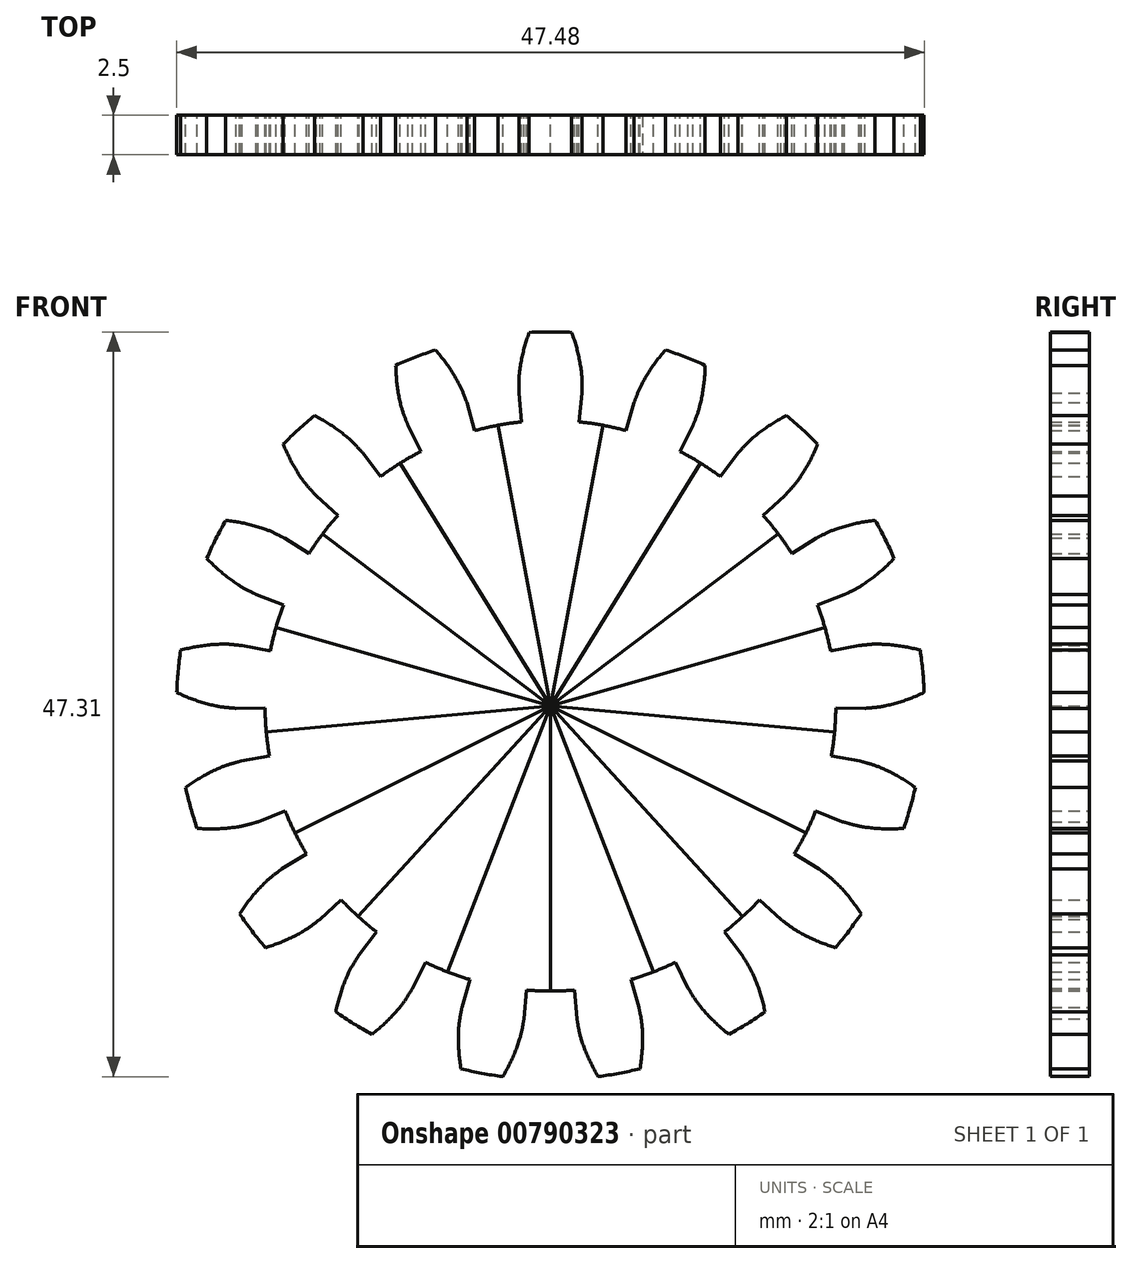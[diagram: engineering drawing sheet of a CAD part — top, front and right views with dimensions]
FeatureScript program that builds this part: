
annotation { "Feature Type Name" : "Feature", "Feature Type Description" : "" }
export const myFeature = defineFeature(function(context is Context, id is Id, definition is map)
    precondition{}
    {
        {
            var Q0;
            Q0=qCreatedBy(makeId("Front.planeOp"),FACE);
            var sketch = newSketch(context, id + "F0", { "sketchPlane" : qUnion([Q0])});
            skArc(sketch, "E0", {"start": v(1.97, 21.16) * mm, "mid": v(1.97, 21.16) * mm, "end": v(1.96, 21.16) * mm});
            skArc(sketch, "E1.0", {"start": v(1.35, 23.71) * mm, "mid": v(0, 23.75) * mm, "end": v(-1.35, 23.71) * mm});
            skArc(sketch, "E2.0", {"start": v(3.33, 17.82) * mm, "mid": v(2.58, 17.94) * mm, "end": v(1.83, 18.03) * mm});
            skPoint(sketch, "E3", {"position": v(-1.96, 21.16) * mm});
            skPoint(sketch, "E4", {"position": v(-2.01, 19.87) * mm});
            skFitSpline(sketch, "E5", {"points": [v(-2.01, 19.87) * mm, v(-2, 20.04) * mm, v(-2, 20.55) * mm, v(-1.94, 21.4) * mm, v(-1.71, 22.55) * mm, v(-1.35, 23.71) * mm], "startDerivative": vector(0.13, 1.6) * mm, "endDerivative": vector(1.85, 5.2) * mm});
            skLineSegment(sketch, "E6", {"start": v(-2.01, 19.87) * mm, "end": v(-1.83, 18.03) * mm});
            skLineSegment(sketch, "E7", {"start": v(-1.83, 18.03) * mm, "end": v(-3.33, 17.82) * mm});
            skFitSpline(sketch, "E8.MirrorCS", {"points": [v(2.01, 19.87) * mm, v(2, 20.04) * mm, v(2, 20.55) * mm, v(1.94, 21.4) * mm, v(1.71, 22.55) * mm, v(1.35, 23.71) * mm], "startDerivative": vector(-0.13, 1.6) * mm, "endDerivative": vector(-1.85, 5.2) * mm});
            skLineSegment(sketch, "E9.MirrorCS", {"start": v(1.83, 18.03) * mm, "end": v(3.33, 17.82) * mm});
            skLineSegment(sketch, "E10.MirrorCS", {"start": v(2.01, 19.87) * mm, "end": v(1.83, 18.03) * mm});
            skPoint(sketch, "E11.MirrorP", {"position": v(1.96, 21.16) * mm});
            skLineSegment(sketch, "E12", {"start": v(0, 0) * mm, "end": v(-3.33, 17.82) * mm});
            skLineSegment(sketch, "E13", {"start": v(0, 0) * mm, "end": v(3.33, 17.82) * mm});
            skArc(sketch, "E14.trimOffspring", {"start": v(-1.83, 18.03) * mm, "mid": v(-2.58, 17.94) * mm, "end": v(-3.33, 17.82) * mm});
            skArc(sketch, "E15.trimOffspring", {"start": v(-1.96, 21.16) * mm, "mid": v(-1.97, 21.16) * mm, "end": v(-1.97, 21.16) * mm});
            skSolve(sketch);
        }
        {
            var Q0;
            Q0 = qSketchRegion(id + "F0", true);
            extrude(context, id + "F1", {"entities" : qUnion([Q0]), "depth" : 2.5 * mm, "offsetDistance" : 25 * mm});
        }
        {
            var Q0;
            Q0=makeQuery(id+"F1.opExtrude","SWEPT_BODY",BODY,{"disambiguationData":[OSD([sQuery(id+"F0.wireOp",EDGE,"E1.0"),sQuery(id+"F0.wireOp",EDGE,"E2.0"),sQuery(id+"F0.wireOp",EDGE,"E5"),sQuery(id+"F0.wireOp",EDGE,"E6"),sQuery(id+"F0.wireOp",EDGE,"E8.MirrorCS"),sQuery(id+"F0.wireOp",EDGE,"E10.MirrorCS"),sQuery(id+"F0.wireOp",EDGE,"E12"),sQuery(id+"F0.wireOp",EDGE,"E13"),sQuery(id+"F0.wireOp",EDGE,"E14.trimOffspring")])]});
            var Q1;
            Q1=makeQuery(id+"F1.opExtrude","SWEPT_EDGE",EDGE,{"disambiguationData":[OSD([sQuery(id+"F0.wireOp",EDGE,"E12"),sQuery(id+"F0.wireOp",EDGE,"E13")])]});
            circularPattern(context, id + "F2", {"entities" : qUnion([Q0]), "axis" : qUnion([Q1]), "angle" : 360 * degree, "instanceCount" : 17, "equalSpace" : true});
        }
    });
